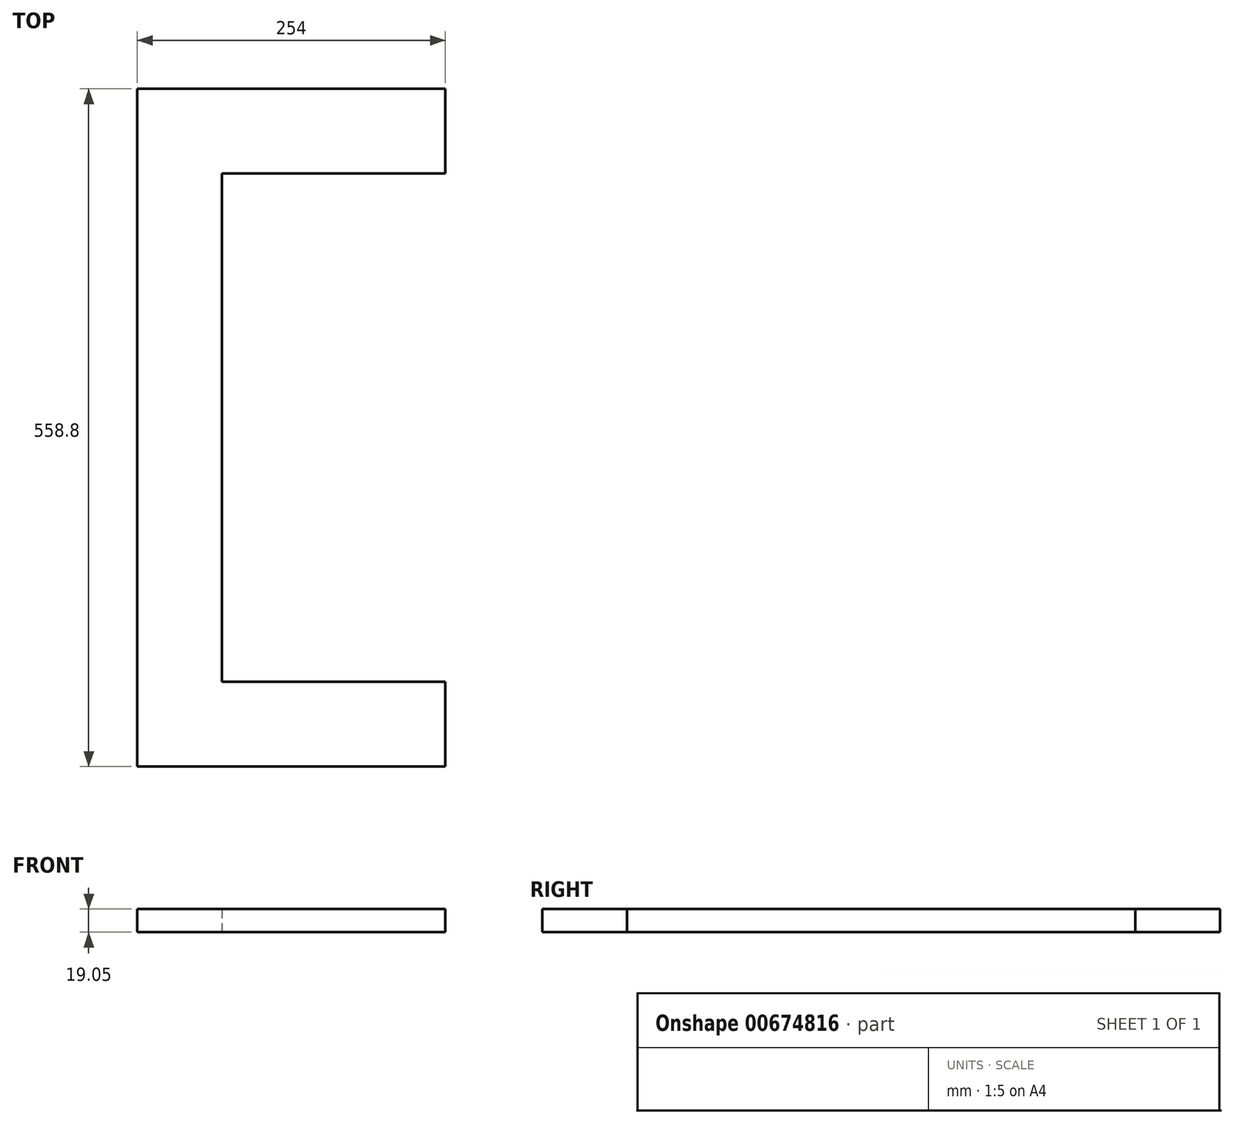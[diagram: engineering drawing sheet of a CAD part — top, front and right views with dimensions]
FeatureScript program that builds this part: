
annotation { "Feature Type Name" : "Feature", "Feature Type Description" : "" }
export const myFeature = defineFeature(function(context is Context, id is Id, definition is map)
    precondition{}
    {
        {
            var Q0;
            Q0=qCreatedBy(makeId("Top.planeOp"),FACE);
            var sketch = newSketch(context, id + "F0", { "sketchPlane" : qUnion([Q0])});
            skLineSegment(sketch, "E0.bottom", {"start": v(-127, 279.4) * mm, "end": v(127, 279.4) * mm});
            skLineSegment(sketch, "E0.top", {"start": v(-127, -279.4) * mm, "end": v(127, -279.4) * mm});
            skLineSegment(sketch, "E0.left", {"start": v(-127, 279.4) * mm, "end": v(-127, -279.4) * mm});
            skLineSegment(sketch, "E0.right", {"start": v(127, 279.4) * mm, "end": v(127, -279.4) * mm});
            skPoint(sketch, "E0.middle", {"position": v(0, 0) * mm});
            skLineSegment(sketch, "E1", {"start": v(127, -279.4) * mm, "end": v(127, -209.55) * mm});
            skLineSegment(sketch, "E2", {"start": v(127, 279.4) * mm, "end": v(127, 209.55) * mm});
            skLineSegment(sketch, "E3", {"start": v(127, -209.55) * mm, "end": v(-57.15, -209.55) * mm});
            skLineSegment(sketch, "E4", {"start": v(127, 209.55) * mm, "end": v(-57.15, 209.55) * mm});
            skLineSegment(sketch, "E5", {"start": v(-57.15, -209.55) * mm, "end": v(-127, -209.55) * mm});
            skLineSegment(sketch, "E6", {"start": v(-57.15, -209.55) * mm, "end": v(-57.15, 209.55) * mm});
            skSolve(sketch);
        }
        {
            var Q0;
            {var subQ1=sQuery(id+"F0.wireOp",EDGE,"E0.top");Q0=makeQuery(id+"F0.imprint","IMPRINT",FACE,{"disambiguationData":[TD([[makeQuery(id+"F0.imprint","IMPRINT",EDGE,{"derivedFrom":subQ1}),1.0]])]});}
            var Q1;
            {var subQ1=sQuery(id+"F0.wireOp",EDGE,"E0.bottom");Q1=makeQuery(id+"F0.imprint","IMPRINT",FACE,{"disambiguationData":[TD([[makeQuery(id+"F0.imprint","IMPRINT",EDGE,{"derivedFrom":subQ1}),-1.0]])]});}
            extrude(context, id + "F1", {"entities" : qUnion([Q0, Q1]), "depth" : 19.05 * mm, "offsetDistance" : 25.4 * mm});
        }
    });
